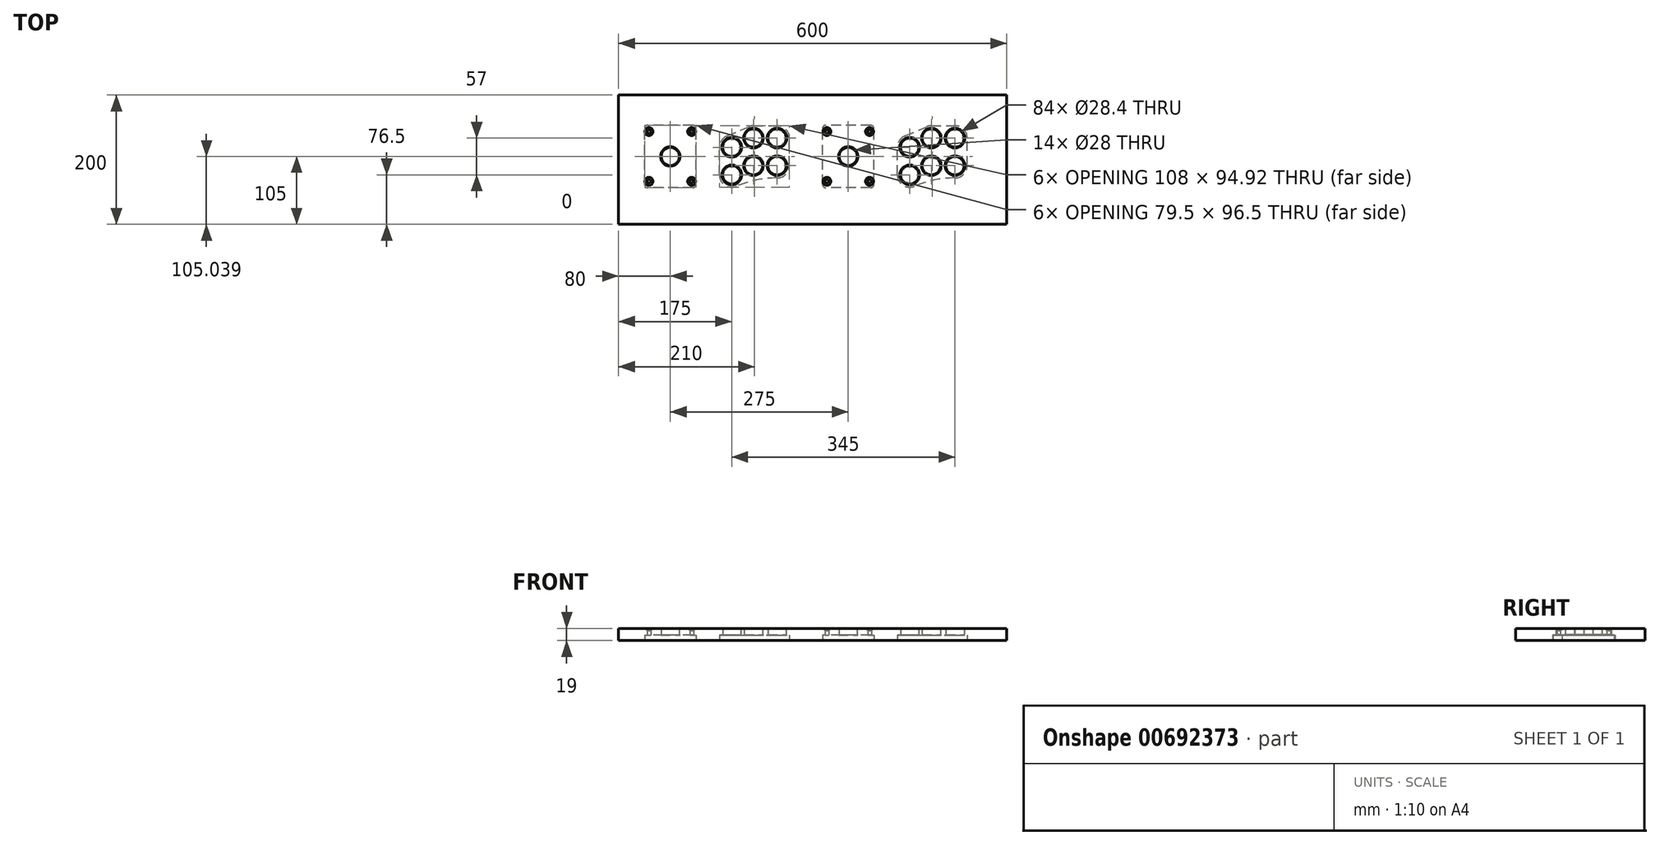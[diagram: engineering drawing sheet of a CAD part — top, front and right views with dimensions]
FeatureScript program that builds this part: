
annotation { "Feature Type Name" : "Feature", "Feature Type Description" : "" }
export const myFeature = defineFeature(function(context is Context, id is Id, definition is map)
    precondition{}
    {
        {
            var Q0;
            Q0=qCreatedBy(makeId("Top.planeOp"),FACE);
            var sketch = newSketch(context, id + "F0", { "sketchPlane" : qUnion([Q0])});
            skLineSegment(sketch, "E0.bottom", {"start": v(-300, 100) * mm, "end": v(300, 100) * mm});
            skLineSegment(sketch, "E0.top", {"start": v(-300, -100) * mm, "end": v(300, -100) * mm});
            skLineSegment(sketch, "E0.left", {"start": v(-300, 100) * mm, "end": v(-300, -100) * mm});
            skLineSegment(sketch, "E0.right", {"start": v(300, 100) * mm, "end": v(300, -100) * mm});
            skPoint(sketch, "E0.middle", {"position": v(0, 0) * mm});
            skLineSegment(sketch, "E1", {"start": v(-300, 19.25) * mm, "end": v(300, 19.25) * mm, "construction": true});
            skLineSegment(sketch, "E2", {"start": v(-300, 33.5) * mm, "end": v(300, 33.5) * mm, "construction": true});
            skLineSegment(sketch, "E3", {"start": v(-300, 5) * mm, "end": v(300, 5) * mm, "construction": true});
            skLineSegment(sketch, "E4", {"start": v(-300, -23.5) * mm, "end": v(300, -23.5) * mm, "construction": true});
            skLineSegment(sketch, "E5", {"start": v(-300, -9.25) * mm, "end": v(300, -9.25) * mm, "construction": true});
            skLineSegment(sketch, "E6", {"start": v(-220, 100) * mm, "end": v(-220, -100) * mm, "construction": true});
            skLineSegment(sketch, "E7", {"start": v(-125, 100) * mm, "end": v(-125, -100) * mm, "construction": true});
            skLineSegment(sketch, "E8", {"start": v(-91.5, 100) * mm, "end": v(-91.5, -100) * mm, "construction": true});
            skLineSegment(sketch, "E9", {"start": v(-55, 100) * mm, "end": v(-55, -100) * mm, "construction": true});
            skCircle(sketch, "E10", {"center": v(-220, 5) * mm, "radius": 14 * mm});
            skCircle(sketch, "E11", {"center": v(-125, 19.25) * mm, "radius": 14.2 * mm});
            skCircle(sketch, "E12", {"center": v(-125, -23.5) * mm, "radius": 14.2 * mm});
            skCircle(sketch, "E13", {"center": v(-91.5, 33.5) * mm, "radius": 14.2 * mm});
            skCircle(sketch, "E14", {"center": v(-91.5, -9.25) * mm, "radius": 14.2 * mm});
            skCircle(sketch, "E15", {"center": v(-55, 33.5) * mm, "radius": 14.2 * mm});
            skCircle(sketch, "E16", {"center": v(-55, -9.25) * mm, "radius": 14.2 * mm});
            skLineSegment(sketch, "E17", {"start": v(55, 100) * mm, "end": v(55, -100) * mm, "construction": true});
            skLineSegment(sketch, "E18", {"start": v(150, 100) * mm, "end": v(150, -100) * mm, "construction": true});
            skLineSegment(sketch, "E19", {"start": v(183.5, 100) * mm, "end": v(183.5, -100) * mm, "construction": true});
            skLineSegment(sketch, "E20", {"start": v(220, 100) * mm, "end": v(220, -100) * mm, "construction": true});
            skLineSegment(sketch, "E21", {"start": v(-220, 90) * mm, "end": v(-300, 90) * mm, "construction": true});
            skLineSegment(sketch, "E22", {"start": v(220, 90) * mm, "end": v(300, 90) * mm, "construction": true});
            skCircle(sketch, "E23", {"center": v(55, 5) * mm, "radius": 14 * mm});
            skCircle(sketch, "E24", {"center": v(150, 19.25) * mm, "radius": 14.2 * mm});
            skCircle(sketch, "E25", {"center": v(150, -23.5) * mm, "radius": 14.2 * mm});
            skCircle(sketch, "E26", {"center": v(183.5, 33.5) * mm, "radius": 14.2 * mm});
            skCircle(sketch, "E27", {"center": v(183.5, -9.25) * mm, "radius": 14.2 * mm});
            skCircle(sketch, "E28", {"center": v(220, -9.25) * mm, "radius": 14.2 * mm});
            skCircle(sketch, "E29", {"center": v(220, 33.5) * mm, "radius": 14.2 * mm});
            skSolve(sketch);
        }
        {
            var Q0;
            Q0=makeQuery(id+"F0.imprint","IMPRINT",FACE,{"disambiguationData":[TD([[makeQuery(id+"F0.imprint","IMPRINT",EDGE,{"derivedFrom":sQuery(id+"F0.wireOp",EDGE,"E0.bottom")}),-1.0]])]});
            extrude(context, id + "F1", {"entities" : qUnion([Q0]), "depth" : 19 * mm, "offsetDistance" : 25 * mm});
        }
        {
            var Q0;
            Q0=makeQuery(id+"F1.opExtrude","CAP_FACE",FACE,{"disambiguationData":[OSD([sQuery(id+"F0.wireOp",EDGE,"E0.bottom"),sQuery(id+"F0.wireOp",EDGE,"E0.top"),sQuery(id+"F0.wireOp",EDGE,"E0.left"),sQuery(id+"F0.wireOp",EDGE,"E0.right"),sQuery(id+"F0.wireOp",EDGE,"E10"),sQuery(id+"F0.wireOp",EDGE,"E11"),sQuery(id+"F0.wireOp",EDGE,"E12"),sQuery(id+"F0.wireOp",EDGE,"E13"),sQuery(id+"F0.wireOp",EDGE,"E14"),sQuery(id+"F0.wireOp",EDGE,"E15"),sQuery(id+"F0.wireOp",EDGE,"E16"),sQuery(id+"F0.wireOp",EDGE,"E23"),sQuery(id+"F0.wireOp",EDGE,"E24"),sQuery(id+"F0.wireOp",EDGE,"E25"),sQuery(id+"F0.wireOp",EDGE,"E26"),sQuery(id+"F0.wireOp",EDGE,"E27"),sQuery(id+"F0.wireOp",EDGE,"E28"),sQuery(id+"F0.wireOp",EDGE,"E29")])],"isStart":true});
            var sketch = newSketch(context, id + "F2", { "sketchPlane" : qUnion([Q0])});
            skLineSegment(sketch, "E30.bottom", {"start": v(-180.25, 43.25) * mm, "end": v(-259.75, 43.25) * mm});
            skLineSegment(sketch, "E30.top", {"start": v(-180.25, -53.25) * mm, "end": v(-259.75, -53.25) * mm});
            skLineSegment(sketch, "E30.left", {"start": v(-180.25, 43.25) * mm, "end": v(-180.25, -53.25) * mm});
            skLineSegment(sketch, "E30.right", {"start": v(-259.75, 43.25) * mm, "end": v(-259.75, -53.25) * mm});
            skPoint(sketch, "E30.middle", {"position": v(-220, -5) * mm});
            skLineSegment(sketch, "E31.bottom", {"start": v(-187, 33.5) * mm, "end": v(-253, 33.5) * mm, "construction": true});
            skLineSegment(sketch, "E31.top", {"start": v(-187, -43.5) * mm, "end": v(-253, -43.5) * mm, "construction": true});
            skLineSegment(sketch, "E31.left", {"start": v(-187, 33.5) * mm, "end": v(-187, -43.5) * mm, "construction": true});
            skLineSegment(sketch, "E31.right", {"start": v(-253, 33.5) * mm, "end": v(-253, -43.5) * mm, "construction": true});
            skCircle(sketch, "E32", {"center": v(-253, 33.5) * mm, "radius": 2.75 * mm});
            skCircle(sketch, "E33", {"center": v(-187, 33.5) * mm, "radius": 2.75 * mm});
            skCircle(sketch, "E34", {"center": v(-187, -43.5) * mm, "radius": 2.75 * mm});
            skCircle(sketch, "E35", {"center": v(-253, -43.5) * mm, "radius": 2.75 * mm});
            skCircle(sketch, "E36", {"center": v(-125, 23.5) * mm, "radius": 19 * mm, "construction": true});
            skCircle(sketch, "E37", {"center": v(-125, -19.25) * mm, "radius": 19 * mm, "construction": true});
            skCircle(sketch, "E38", {"center": v(-91.5, -33.5) * mm, "radius": 19 * mm, "construction": true});
            skCircle(sketch, "E39", {"center": v(-55, -33.5) * mm, "radius": 19 * mm, "construction": true});
            skCircle(sketch, "E40", {"center": v(-55, 9.25) * mm, "radius": 19 * mm, "construction": true});
            skCircle(sketch, "E41", {"center": v(-91.5, 9.25) * mm, "radius": 19 * mm, "construction": true});
            skLineSegment(sketch, "E42", {"start": v(-91.5, -52.5) * mm, "end": v(-55, -52.5) * mm});
            skLineSegment(sketch, "E43", {"start": v(-132.44, -36.73) * mm, "end": v(-98.94, -50.98) * mm});
            skLineSegment(sketch, "E44", {"start": v(-144, 23.5) * mm, "end": v(-144, -19.25) * mm});
            skLineSegment(sketch, "E45", {"start": v(-117.56, 40.98) * mm, "end": v(-84.06, 26.73) * mm, "construction": true});
            skLineSegment(sketch, "E46", {"start": v(-91.5, 28.25) * mm, "end": v(-55, 28.25) * mm, "construction": true});
            skLineSegment(sketch, "E47", {"start": v(-36, 9.25) * mm, "end": v(-36, -33.5) * mm});
            skArc(sketch, "E48", {"start": v(-117.56, 40.98) * mm, "mid": v(-135.48, 39.35) * mm, "end": v(-144, 23.5) * mm});
            skArc(sketch, "E49", {"start": v(-91.5, 28.25) * mm, "mid": v(-95.3, -9.37) * mm, "end": v(-84.06, 26.73) * mm});
            skArc(sketch, "E50", {"start": v(-36, 9.25) * mm, "mid": v(-41.56, 22.69) * mm, "end": v(-55, 28.25) * mm});
            skArc(sketch, "E51", {"start": v(-55, -52.5) * mm, "mid": v(-41.56, -46.94) * mm, "end": v(-36, -33.5) * mm});
            skArc(sketch, "E52", {"start": v(-144, -19.25) * mm, "mid": v(-140.85, -29.73) * mm, "end": v(-132.44, -36.73) * mm});
            skLineSegment(sketch, "E53.bottom", {"start": v(94.75, 43.25) * mm, "end": v(15.25, 43.25) * mm});
            skLineSegment(sketch, "E53.top", {"start": v(94.75, -53.25) * mm, "end": v(15.25, -53.25) * mm});
            skLineSegment(sketch, "E53.left", {"start": v(94.75, 43.25) * mm, "end": v(94.75, -53.25) * mm});
            skLineSegment(sketch, "E53.right", {"start": v(15.25, 43.25) * mm, "end": v(15.25, -53.25) * mm});
            skPoint(sketch, "E53.middle", {"position": v(55, -5) * mm});
            skLineSegment(sketch, "E54.bottom", {"start": v(88, 33.5) * mm, "end": v(22, 33.5) * mm, "construction": true});
            skLineSegment(sketch, "E54.top", {"start": v(88, -43.5) * mm, "end": v(22, -43.5) * mm, "construction": true});
            skLineSegment(sketch, "E54.left", {"start": v(88, 33.5) * mm, "end": v(88, -43.5) * mm, "construction": true});
            skLineSegment(sketch, "E54.right", {"start": v(22, 33.5) * mm, "end": v(22, -43.5) * mm, "construction": true});
            skCircle(sketch, "E55", {"center": v(150, 23.5) * mm, "radius": 19 * mm, "construction": true});
            skCircle(sketch, "E56", {"center": v(183.5, 9.25) * mm, "radius": 19 * mm, "construction": true});
            skCircle(sketch, "E57", {"center": v(220, 9.25) * mm, "radius": 19 * mm, "construction": true});
            skCircle(sketch, "E58", {"center": v(220, -33.5) * mm, "radius": 19 * mm, "construction": true});
            skCircle(sketch, "E59", {"center": v(183.5, -33.5) * mm, "radius": 19 * mm, "construction": true});
            skCircle(sketch, "E60", {"center": v(150, -19.25) * mm, "radius": 19 * mm, "construction": true});
            skCircle(sketch, "E61", {"center": v(22, 33.5) * mm, "radius": 2.75 * mm});
            skCircle(sketch, "E62", {"center": v(88, 33.5) * mm, "radius": 2.75 * mm});
            skCircle(sketch, "E63", {"center": v(88, -43.5) * mm, "radius": 2.75 * mm});
            skCircle(sketch, "E64", {"center": v(22, -43.5) * mm, "radius": 2.75 * mm});
            skLineSegment(sketch, "E65", {"start": v(142.56, -36.73) * mm, "end": v(176.06, -50.98) * mm});
            skLineSegment(sketch, "E66", {"start": v(183.5, -52.5) * mm, "end": v(220, -52.5) * mm});
            skLineSegment(sketch, "E67", {"start": v(131, 23.5) * mm, "end": v(131, -19.25) * mm});
            skLineSegment(sketch, "E68", {"start": v(157.44, 40.98) * mm, "end": v(190.94, 26.73) * mm, "construction": true});
            skLineSegment(sketch, "E69", {"start": v(183.5, 28.25) * mm, "end": v(220, 28.25) * mm, "construction": true});
            skLineSegment(sketch, "E70", {"start": v(239, 9.25) * mm, "end": v(239, -33.5) * mm});
            skArc(sketch, "E71", {"start": v(220, -52.5) * mm, "mid": v(233.44, -46.94) * mm, "end": v(239, -33.5) * mm});
            skArc(sketch, "E72", {"start": v(239, 9.25) * mm, "mid": v(233.44, 22.69) * mm, "end": v(220, 28.25) * mm});
            skArc(sketch, "E73", {"start": v(183.5, 28.25) * mm, "mid": v(179.7, -9.37) * mm, "end": v(190.94, 26.73) * mm});
            skArc(sketch, "E74", {"start": v(157.44, 40.98) * mm, "mid": v(139.52, 39.35) * mm, "end": v(131, 23.5) * mm});
            skArc(sketch, "E75", {"start": v(131, -19.25) * mm, "mid": v(134.15, -29.73) * mm, "end": v(142.56, -36.73) * mm});
            skArc(sketch, "E76", {"start": v(-117.56, 40.98) * mm, "mid": v(-86.92, 31.47) * mm, "end": v(-55, 28.25) * mm});
            skArc(sketch, "E77", {"start": v(-98.94, -50.98) * mm, "mid": v(-95.3, -52.12) * mm, "end": v(-91.5, -52.5) * mm});
            skArc(sketch, "E78", {"start": v(157.44, 40.98) * mm, "mid": v(188.08, 31.47) * mm, "end": v(220, 28.25) * mm});
            skArc(sketch, "E79", {"start": v(176.06, -50.98) * mm, "mid": v(179.7, -52.12) * mm, "end": v(183.5, -52.5) * mm});
            skSolve(sketch);
        }
        {
            var Q0;
            Q0=makeQuery(id+"F2.imprint","IMPRINT",FACE,{"disambiguationData":[TD([[makeQuery(id+"F2.imprint","IMPRINT",EDGE,{"derivedFrom":sQuery(id+"F2.wireOp",EDGE,"E44")}),1.0]])]});
            var Q1;
            Q1=makeQuery(id+"F2.imprint","IMPRINT",FACE,{"disambiguationData":[TD([[makeQuery(id+"F2.imprint","IMPRINT",EDGE,{"derivedFrom":sQuery(id+"F2.wireOp",EDGE,"E32")}),1.0]])]});
            var Q2;
            Q2=makeQuery(id+"F2.imprint","IMPRINT",FACE,{"disambiguationData":[TD([[makeQuery(id+"F2.imprint","IMPRINT",EDGE,{"derivedFrom":sQuery(id+"F2.wireOp",EDGE,"E33")}),1.0]])]});
            var Q3;
            Q3=makeQuery(id+"F2.imprint","IMPRINT",FACE,{"disambiguationData":[TD([[makeQuery(id+"F2.imprint","IMPRINT",EDGE,{"derivedFrom":sQuery(id+"F2.wireOp",EDGE,"E34")}),1.0]])]});
            var Q4;
            Q4=makeQuery(id+"F2.imprint","IMPRINT",FACE,{"disambiguationData":[TD([[makeQuery(id+"F2.imprint","IMPRINT",EDGE,{"derivedFrom":sQuery(id+"F2.wireOp",EDGE,"E35")}),1.0]])]});
            var Q5;
            Q5=makeQuery(id+"F2.imprint","IMPRINT",FACE,{"disambiguationData":[TD([[makeQuery(id+"F2.imprint","IMPRINT",EDGE,{"derivedFrom":sQuery(id+"F2.wireOp",EDGE,"E30.bottom")}),1.0]])]});
            var Q6;
            Q6=makeQuery(id+"F2.imprint","IMPRINT",FACE,{"disambiguationData":[TD([[makeQuery(id+"F2.imprint","IMPRINT",EDGE,{"derivedFrom":sQuery(id+"F2.wireOp",EDGE,"E61")}),1.0]])]});
            var Q7;
            Q7=makeQuery(id+"F2.imprint","IMPRINT",FACE,{"disambiguationData":[TD([[makeQuery(id+"F2.imprint","IMPRINT",EDGE,{"derivedFrom":sQuery(id+"F2.wireOp",EDGE,"E62")}),1.0]])]});
            var Q8;
            Q8=makeQuery(id+"F2.imprint","IMPRINT",FACE,{"disambiguationData":[TD([[makeQuery(id+"F2.imprint","IMPRINT",EDGE,{"derivedFrom":sQuery(id+"F2.wireOp",EDGE,"E63")}),1.0]])]});
            var Q9;
            Q9=makeQuery(id+"F2.imprint","IMPRINT",FACE,{"disambiguationData":[TD([[makeQuery(id+"F2.imprint","IMPRINT",EDGE,{"derivedFrom":sQuery(id+"F2.wireOp",EDGE,"E64")}),1.0]])]});
            var Q10;
            Q10=makeQuery(id+"F2.imprint","IMPRINT",FACE,{"disambiguationData":[TD([[makeQuery(id+"F2.imprint","IMPRINT",EDGE,{"derivedFrom":sQuery(id+"F2.wireOp",EDGE,"E53.bottom")}),1.0]])]});
            var Q11;
            Q11=makeQuery(id+"F2.imprint","IMPRINT",FACE,{"disambiguationData":[TD([[makeQuery(id+"F2.imprint","IMPRINT",EDGE,{"derivedFrom":sQuery(id+"F2.wireOp",EDGE,"E67")}),1.0]])]});
            extrude(context, id + "F3", {"entities" : qUnion([Q0, Q1, Q2, Q3, Q4, Q5, Q6, Q7, Q8, Q9, Q10, Q11]), "operationType" : NewBodyOperationType.REMOVE, "oppositeDirection" : true, "depth" : 8.5 * mm, "offsetDistance" : 25 * mm});
        }
        {
            var Q0;
            Q0=makeQuery(id+"F2.imprint","IMPRINT",FACE,{"disambiguationData":[TD([[makeQuery(id+"F2.imprint","IMPRINT",EDGE,{"derivedFrom":sQuery(id+"F2.wireOp",EDGE,"E32")}),1.0]])]});
            var Q1;
            Q1=makeQuery(id+"F2.imprint","IMPRINT",FACE,{"disambiguationData":[TD([[makeQuery(id+"F2.imprint","IMPRINT",EDGE,{"derivedFrom":sQuery(id+"F2.wireOp",EDGE,"E33")}),1.0]])]});
            var Q2;
            Q2=makeQuery(id+"F2.imprint","IMPRINT",FACE,{"disambiguationData":[TD([[makeQuery(id+"F2.imprint","IMPRINT",EDGE,{"derivedFrom":sQuery(id+"F2.wireOp",EDGE,"E34")}),1.0]])]});
            var Q3;
            Q3=makeQuery(id+"F2.imprint","IMPRINT",FACE,{"disambiguationData":[TD([[makeQuery(id+"F2.imprint","IMPRINT",EDGE,{"derivedFrom":sQuery(id+"F2.wireOp",EDGE,"E35")}),1.0]])]});
            var Q4;
            Q4=makeQuery(id+"F2.imprint","IMPRINT",FACE,{"disambiguationData":[TD([[makeQuery(id+"F2.imprint","IMPRINT",EDGE,{"derivedFrom":sQuery(id+"F2.wireOp",EDGE,"E61")}),1.0]])]});
            var Q5;
            Q5=makeQuery(id+"F2.imprint","IMPRINT",FACE,{"disambiguationData":[TD([[makeQuery(id+"F2.imprint","IMPRINT",EDGE,{"derivedFrom":sQuery(id+"F2.wireOp",EDGE,"E62")}),1.0]])]});
            var Q6;
            Q6=makeQuery(id+"F2.imprint","IMPRINT",FACE,{"disambiguationData":[TD([[makeQuery(id+"F2.imprint","IMPRINT",EDGE,{"derivedFrom":sQuery(id+"F2.wireOp",EDGE,"E63")}),1.0]])]});
            var Q7;
            Q7=makeQuery(id+"F2.imprint","IMPRINT",FACE,{"disambiguationData":[TD([[makeQuery(id+"F2.imprint","IMPRINT",EDGE,{"derivedFrom":sQuery(id+"F2.wireOp",EDGE,"E64")}),1.0]])]});
            extrude(context, id + "F4", {"entities" : qUnion([Q0, Q1, Q2, Q3, Q4, Q5, Q6, Q7]), "operationType" : NewBodyOperationType.REMOVE, "endBound" : BoundingType.THROUGH_ALL, "oppositeDirection" : true, "depth" : 25 * mm, "offsetDistance" : 25 * mm});
        }
        {
            var Q0;
            Q0=makeQuery(id+"F3.boolean.opBoolean","COPY",EDGE,{"derivedFrom":makeQuery(id+"F3.opExtrude","SWEPT_EDGE",EDGE,{"disambiguationData":[OSD([sQuery(id+"F2.wireOp",EDGE,"E30.bottom"),sQuery(id+"F2.wireOp",EDGE,"E30.right")])]})});
            var Q1;
            Q1=makeQuery(id+"F3.boolean.opBoolean","COPY",EDGE,{"derivedFrom":makeQuery(id+"F3.opExtrude","SWEPT_EDGE",EDGE,{"disambiguationData":[OSD([sQuery(id+"F2.wireOp",EDGE,"E30.bottom"),sQuery(id+"F2.wireOp",EDGE,"E30.left")])]})});
            var Q2;
            Q2=makeQuery(id+"F3.boolean.opBoolean","COPY",EDGE,{"derivedFrom":makeQuery(id+"F3.opExtrude","SWEPT_EDGE",EDGE,{"disambiguationData":[OSD([sQuery(id+"F2.wireOp",EDGE,"E30.top"),sQuery(id+"F2.wireOp",EDGE,"E30.left")])]})});
            var Q3;
            Q3=makeQuery(id+"F3.boolean.opBoolean","COPY",EDGE,{"derivedFrom":makeQuery(id+"F3.opExtrude","SWEPT_EDGE",EDGE,{"disambiguationData":[OSD([sQuery(id+"F2.wireOp",EDGE,"E30.top"),sQuery(id+"F2.wireOp",EDGE,"E30.right")])]})});
            var Q4;
            Q4=makeQuery(id+"F3.boolean.opBoolean","COPY",EDGE,{"derivedFrom":makeQuery(id+"F3.opExtrude","SWEPT_EDGE",EDGE,{"disambiguationData":[OSD([sQuery(id+"F2.wireOp",EDGE,"E53.top"),sQuery(id+"F2.wireOp",EDGE,"E53.right")])]})});
            var Q5;
            Q5=makeQuery(id+"F3.boolean.opBoolean","COPY",EDGE,{"derivedFrom":makeQuery(id+"F3.opExtrude","SWEPT_EDGE",EDGE,{"disambiguationData":[OSD([sQuery(id+"F2.wireOp",EDGE,"E53.bottom"),sQuery(id+"F2.wireOp",EDGE,"E53.right")])]})});
            var Q6;
            Q6=makeQuery(id+"F3.boolean.opBoolean","COPY",EDGE,{"derivedFrom":makeQuery(id+"F3.opExtrude","SWEPT_EDGE",EDGE,{"disambiguationData":[OSD([sQuery(id+"F2.wireOp",EDGE,"E53.bottom"),sQuery(id+"F2.wireOp",EDGE,"E53.left")])]})});
            var Q7;
            Q7=makeQuery(id+"F3.boolean.opBoolean","COPY",EDGE,{"derivedFrom":makeQuery(id+"F3.opExtrude","SWEPT_EDGE",EDGE,{"disambiguationData":[OSD([sQuery(id+"F2.wireOp",EDGE,"E53.top"),sQuery(id+"F2.wireOp",EDGE,"E53.left")])]})});
            fillet(context, id + "F5", {"entities" : qUnion([Q0, Q1, Q2, Q3, Q4, Q5, Q6, Q7]), "radius" : 5 * mm, "tangentPropagation" : true, "allowEdgeOverflow" : false});
        }
        {
            var Q0;
            Q0=makeQuery(id+"F4.boolean.opBoolean","INTERSECT",EDGE,{"derivedFrom":[makeQuery(id+"F1.opExtrude","CAP_FACE",FACE,{"disambiguationData":[OSD([sQuery(id+"F0.wireOp",EDGE,"E0.bottom"),sQuery(id+"F0.wireOp",EDGE,"E0.top"),sQuery(id+"F0.wireOp",EDGE,"E0.left"),sQuery(id+"F0.wireOp",EDGE,"E0.right"),sQuery(id+"F0.wireOp",EDGE,"E10"),sQuery(id+"F0.wireOp",EDGE,"E11"),sQuery(id+"F0.wireOp",EDGE,"E12"),sQuery(id+"F0.wireOp",EDGE,"E13"),sQuery(id+"F0.wireOp",EDGE,"E14"),sQuery(id+"F0.wireOp",EDGE,"E15"),sQuery(id+"F0.wireOp",EDGE,"E16"),sQuery(id+"F0.wireOp",EDGE,"E23"),sQuery(id+"F0.wireOp",EDGE,"E24"),sQuery(id+"F0.wireOp",EDGE,"E25"),sQuery(id+"F0.wireOp",EDGE,"E26"),sQuery(id+"F0.wireOp",EDGE,"E27"),sQuery(id+"F0.wireOp",EDGE,"E28"),sQuery(id+"F0.wireOp",EDGE,"E29")])],"isStart":false}),makeQuery(id+"F4.opExtrude","SWEPT_FACE",FACE,{"disambiguationData":[OSD([sQuery(id+"F2.wireOp",EDGE,"E62")])]})]});
            var Q1;
            Q1=makeQuery(id+"F4.boolean.opBoolean","INTERSECT",EDGE,{"derivedFrom":[makeQuery(id+"F1.opExtrude","CAP_FACE",FACE,{"disambiguationData":[OSD([sQuery(id+"F0.wireOp",EDGE,"E0.bottom"),sQuery(id+"F0.wireOp",EDGE,"E0.top"),sQuery(id+"F0.wireOp",EDGE,"E0.left"),sQuery(id+"F0.wireOp",EDGE,"E0.right"),sQuery(id+"F0.wireOp",EDGE,"E10"),sQuery(id+"F0.wireOp",EDGE,"E11"),sQuery(id+"F0.wireOp",EDGE,"E12"),sQuery(id+"F0.wireOp",EDGE,"E13"),sQuery(id+"F0.wireOp",EDGE,"E14"),sQuery(id+"F0.wireOp",EDGE,"E15"),sQuery(id+"F0.wireOp",EDGE,"E16"),sQuery(id+"F0.wireOp",EDGE,"E23"),sQuery(id+"F0.wireOp",EDGE,"E24"),sQuery(id+"F0.wireOp",EDGE,"E25"),sQuery(id+"F0.wireOp",EDGE,"E26"),sQuery(id+"F0.wireOp",EDGE,"E27"),sQuery(id+"F0.wireOp",EDGE,"E28"),sQuery(id+"F0.wireOp",EDGE,"E29")])],"isStart":false}),makeQuery(id+"F4.opExtrude","SWEPT_FACE",FACE,{"disambiguationData":[OSD([sQuery(id+"F2.wireOp",EDGE,"E63")])]})]});
            var Q2;
            Q2=makeQuery(id+"F4.boolean.opBoolean","INTERSECT",EDGE,{"derivedFrom":[makeQuery(id+"F1.opExtrude","CAP_FACE",FACE,{"disambiguationData":[OSD([sQuery(id+"F0.wireOp",EDGE,"E0.bottom"),sQuery(id+"F0.wireOp",EDGE,"E0.top"),sQuery(id+"F0.wireOp",EDGE,"E0.left"),sQuery(id+"F0.wireOp",EDGE,"E0.right"),sQuery(id+"F0.wireOp",EDGE,"E10"),sQuery(id+"F0.wireOp",EDGE,"E11"),sQuery(id+"F0.wireOp",EDGE,"E12"),sQuery(id+"F0.wireOp",EDGE,"E13"),sQuery(id+"F0.wireOp",EDGE,"E14"),sQuery(id+"F0.wireOp",EDGE,"E15"),sQuery(id+"F0.wireOp",EDGE,"E16"),sQuery(id+"F0.wireOp",EDGE,"E23"),sQuery(id+"F0.wireOp",EDGE,"E24"),sQuery(id+"F0.wireOp",EDGE,"E25"),sQuery(id+"F0.wireOp",EDGE,"E26"),sQuery(id+"F0.wireOp",EDGE,"E27"),sQuery(id+"F0.wireOp",EDGE,"E28"),sQuery(id+"F0.wireOp",EDGE,"E29")])],"isStart":false}),makeQuery(id+"F4.opExtrude","SWEPT_FACE",FACE,{"disambiguationData":[OSD([sQuery(id+"F2.wireOp",EDGE,"E64")])]})]});
            var Q3;
            Q3=makeQuery(id+"F4.boolean.opBoolean","INTERSECT",EDGE,{"derivedFrom":[makeQuery(id+"F1.opExtrude","CAP_FACE",FACE,{"disambiguationData":[OSD([sQuery(id+"F0.wireOp",EDGE,"E0.bottom"),sQuery(id+"F0.wireOp",EDGE,"E0.top"),sQuery(id+"F0.wireOp",EDGE,"E0.left"),sQuery(id+"F0.wireOp",EDGE,"E0.right"),sQuery(id+"F0.wireOp",EDGE,"E10"),sQuery(id+"F0.wireOp",EDGE,"E11"),sQuery(id+"F0.wireOp",EDGE,"E12"),sQuery(id+"F0.wireOp",EDGE,"E13"),sQuery(id+"F0.wireOp",EDGE,"E14"),sQuery(id+"F0.wireOp",EDGE,"E15"),sQuery(id+"F0.wireOp",EDGE,"E16"),sQuery(id+"F0.wireOp",EDGE,"E23"),sQuery(id+"F0.wireOp",EDGE,"E24"),sQuery(id+"F0.wireOp",EDGE,"E25"),sQuery(id+"F0.wireOp",EDGE,"E26"),sQuery(id+"F0.wireOp",EDGE,"E27"),sQuery(id+"F0.wireOp",EDGE,"E28"),sQuery(id+"F0.wireOp",EDGE,"E29")])],"isStart":false}),makeQuery(id+"F4.opExtrude","SWEPT_FACE",FACE,{"disambiguationData":[OSD([sQuery(id+"F2.wireOp",EDGE,"E61")])]})]});
            var Q4;
            Q4=makeQuery(id+"F4.boolean.opBoolean","INTERSECT",EDGE,{"derivedFrom":[makeQuery(id+"F1.opExtrude","CAP_FACE",FACE,{"disambiguationData":[OSD([sQuery(id+"F0.wireOp",EDGE,"E0.bottom"),sQuery(id+"F0.wireOp",EDGE,"E0.top"),sQuery(id+"F0.wireOp",EDGE,"E0.left"),sQuery(id+"F0.wireOp",EDGE,"E0.right"),sQuery(id+"F0.wireOp",EDGE,"E10"),sQuery(id+"F0.wireOp",EDGE,"E11"),sQuery(id+"F0.wireOp",EDGE,"E12"),sQuery(id+"F0.wireOp",EDGE,"E13"),sQuery(id+"F0.wireOp",EDGE,"E14"),sQuery(id+"F0.wireOp",EDGE,"E15"),sQuery(id+"F0.wireOp",EDGE,"E16"),sQuery(id+"F0.wireOp",EDGE,"E23"),sQuery(id+"F0.wireOp",EDGE,"E24"),sQuery(id+"F0.wireOp",EDGE,"E25"),sQuery(id+"F0.wireOp",EDGE,"E26"),sQuery(id+"F0.wireOp",EDGE,"E27"),sQuery(id+"F0.wireOp",EDGE,"E28"),sQuery(id+"F0.wireOp",EDGE,"E29")])],"isStart":false}),makeQuery(id+"F4.opExtrude","SWEPT_FACE",FACE,{"disambiguationData":[OSD([sQuery(id+"F2.wireOp",EDGE,"E34")])]})]});
            var Q5;
            Q5=makeQuery(id+"F4.boolean.opBoolean","INTERSECT",EDGE,{"derivedFrom":[makeQuery(id+"F1.opExtrude","CAP_FACE",FACE,{"disambiguationData":[OSD([sQuery(id+"F0.wireOp",EDGE,"E0.bottom"),sQuery(id+"F0.wireOp",EDGE,"E0.top"),sQuery(id+"F0.wireOp",EDGE,"E0.left"),sQuery(id+"F0.wireOp",EDGE,"E0.right"),sQuery(id+"F0.wireOp",EDGE,"E10"),sQuery(id+"F0.wireOp",EDGE,"E11"),sQuery(id+"F0.wireOp",EDGE,"E12"),sQuery(id+"F0.wireOp",EDGE,"E13"),sQuery(id+"F0.wireOp",EDGE,"E14"),sQuery(id+"F0.wireOp",EDGE,"E15"),sQuery(id+"F0.wireOp",EDGE,"E16"),sQuery(id+"F0.wireOp",EDGE,"E23"),sQuery(id+"F0.wireOp",EDGE,"E24"),sQuery(id+"F0.wireOp",EDGE,"E25"),sQuery(id+"F0.wireOp",EDGE,"E26"),sQuery(id+"F0.wireOp",EDGE,"E27"),sQuery(id+"F0.wireOp",EDGE,"E28"),sQuery(id+"F0.wireOp",EDGE,"E29")])],"isStart":false}),makeQuery(id+"F4.opExtrude","SWEPT_FACE",FACE,{"disambiguationData":[OSD([sQuery(id+"F2.wireOp",EDGE,"E33")])]})]});
            var Q6;
            Q6=makeQuery(id+"F4.boolean.opBoolean","INTERSECT",EDGE,{"derivedFrom":[makeQuery(id+"F1.opExtrude","CAP_FACE",FACE,{"disambiguationData":[OSD([sQuery(id+"F0.wireOp",EDGE,"E0.bottom"),sQuery(id+"F0.wireOp",EDGE,"E0.top"),sQuery(id+"F0.wireOp",EDGE,"E0.left"),sQuery(id+"F0.wireOp",EDGE,"E0.right"),sQuery(id+"F0.wireOp",EDGE,"E10"),sQuery(id+"F0.wireOp",EDGE,"E11"),sQuery(id+"F0.wireOp",EDGE,"E12"),sQuery(id+"F0.wireOp",EDGE,"E13"),sQuery(id+"F0.wireOp",EDGE,"E14"),sQuery(id+"F0.wireOp",EDGE,"E15"),sQuery(id+"F0.wireOp",EDGE,"E16"),sQuery(id+"F0.wireOp",EDGE,"E23"),sQuery(id+"F0.wireOp",EDGE,"E24"),sQuery(id+"F0.wireOp",EDGE,"E25"),sQuery(id+"F0.wireOp",EDGE,"E26"),sQuery(id+"F0.wireOp",EDGE,"E27"),sQuery(id+"F0.wireOp",EDGE,"E28"),sQuery(id+"F0.wireOp",EDGE,"E29")])],"isStart":false}),makeQuery(id+"F4.opExtrude","SWEPT_FACE",FACE,{"disambiguationData":[OSD([sQuery(id+"F2.wireOp",EDGE,"E32")])]})]});
            var Q7;
            Q7=makeQuery(id+"F4.boolean.opBoolean","INTERSECT",EDGE,{"derivedFrom":[makeQuery(id+"F1.opExtrude","CAP_FACE",FACE,{"disambiguationData":[OSD([sQuery(id+"F0.wireOp",EDGE,"E0.bottom"),sQuery(id+"F0.wireOp",EDGE,"E0.top"),sQuery(id+"F0.wireOp",EDGE,"E0.left"),sQuery(id+"F0.wireOp",EDGE,"E0.right"),sQuery(id+"F0.wireOp",EDGE,"E10"),sQuery(id+"F0.wireOp",EDGE,"E11"),sQuery(id+"F0.wireOp",EDGE,"E12"),sQuery(id+"F0.wireOp",EDGE,"E13"),sQuery(id+"F0.wireOp",EDGE,"E14"),sQuery(id+"F0.wireOp",EDGE,"E15"),sQuery(id+"F0.wireOp",EDGE,"E16"),sQuery(id+"F0.wireOp",EDGE,"E23"),sQuery(id+"F0.wireOp",EDGE,"E24"),sQuery(id+"F0.wireOp",EDGE,"E25"),sQuery(id+"F0.wireOp",EDGE,"E26"),sQuery(id+"F0.wireOp",EDGE,"E27"),sQuery(id+"F0.wireOp",EDGE,"E28"),sQuery(id+"F0.wireOp",EDGE,"E29")])],"isStart":false}),makeQuery(id+"F4.opExtrude","SWEPT_FACE",FACE,{"disambiguationData":[OSD([sQuery(id+"F2.wireOp",EDGE,"E35")])]})]});
            chamfer(context, id + "F6", {"entities" : qUnion([Q0, Q1, Q2, Q3, Q4, Q5, Q6, Q7]), "width" : 3.5 * mm, "tangentPropagation" : true});
        }
        {
            var Q0;
            Q0=makeQuery(id+"F1.opExtrude","SWEPT_FACE",FACE,{"disambiguationData":[OSD([sQuery(id+"F0.wireOp",EDGE,"E10")])]});
            var Q1;
            Q1=makeQuery(id+"F1.opExtrude","SWEPT_FACE",FACE,{"disambiguationData":[OSD([sQuery(id+"F0.wireOp",EDGE,"E11")])]});
            var Q2;
            Q2=makeQuery(id+"F1.opExtrude","SWEPT_FACE",FACE,{"disambiguationData":[OSD([sQuery(id+"F0.wireOp",EDGE,"E13")])]});
            var Q3;
            Q3=makeQuery(id+"F1.opExtrude","SWEPT_FACE",FACE,{"disambiguationData":[OSD([sQuery(id+"F0.wireOp",EDGE,"E12")])]});
            var Q4;
            Q4=makeQuery(id+"F1.opExtrude","SWEPT_FACE",FACE,{"disambiguationData":[OSD([sQuery(id+"F0.wireOp",EDGE,"E14")])]});
            var Q5;
            Q5=makeQuery(id+"F1.opExtrude","SWEPT_FACE",FACE,{"disambiguationData":[OSD([sQuery(id+"F0.wireOp",EDGE,"E16")])]});
            var Q6;
            Q6=makeQuery(id+"F1.opExtrude","SWEPT_FACE",FACE,{"disambiguationData":[OSD([sQuery(id+"F0.wireOp",EDGE,"E15")])]});
            var Q7;
            Q7=makeQuery(id+"F1.opExtrude","SWEPT_FACE",FACE,{"disambiguationData":[OSD([sQuery(id+"F0.wireOp",EDGE,"E23")])]});
            var Q8;
            Q8=makeQuery(id+"F1.opExtrude","SWEPT_FACE",FACE,{"disambiguationData":[OSD([sQuery(id+"F0.wireOp",EDGE,"E24")])]});
            var Q9;
            Q9=makeQuery(id+"F1.opExtrude","SWEPT_FACE",FACE,{"disambiguationData":[OSD([sQuery(id+"F0.wireOp",EDGE,"E25")])]});
            var Q10;
            Q10=makeQuery(id+"F1.opExtrude","SWEPT_FACE",FACE,{"disambiguationData":[OSD([sQuery(id+"F0.wireOp",EDGE,"E27")])]});
            var Q11;
            Q11=makeQuery(id+"F1.opExtrude","SWEPT_FACE",FACE,{"disambiguationData":[OSD([sQuery(id+"F0.wireOp",EDGE,"E26")])]});
            var Q12;
            Q12=makeQuery(id+"F1.opExtrude","SWEPT_FACE",FACE,{"disambiguationData":[OSD([sQuery(id+"F0.wireOp",EDGE,"E29")])]});
            var Q13;
            Q13=makeQuery(id+"F1.opExtrude","SWEPT_FACE",FACE,{"disambiguationData":[OSD([sQuery(id+"F0.wireOp",EDGE,"E28")])]});
            var Q14;
            Q14=makeQuery(id+"F3.boolean.opBoolean","COPY",EDGE,{"derivedFrom":makeQuery(id+"F3.opExtrude","CAP_EDGE",EDGE,{"disambiguationData":[OSD([sQuery(id+"F2.wireOp",EDGE,"RX0PKqlT-ShXH-tcj8-fC1a-jLyNVPEMgFMR")])],"isStart":true})});
            var Q15;
            Q15=makeQuery(id+"F3.boolean.opBoolean","COPY",EDGE,{"derivedFrom":makeQuery(id+"F3.opExtrude","CAP_EDGE",EDGE,{"disambiguationData":[OSD([sQuery(id+"F2.wireOp",EDGE,"E53.top")])],"isStart":true})});
            var Q16;
            Q16=makeQuery(id+"F3.boolean.opBoolean","COPY",EDGE,{"derivedFrom":makeQuery(id+"F3.opExtrude","CAP_EDGE",EDGE,{"disambiguationData":[OSD([sQuery(id+"F2.wireOp",EDGE,"N9enReF0-IvZI-JQNr-NccO-0kK5CmvpcBLG")])],"isStart":true})});
            var Q17;
            Q17=makeQuery(id+"F3.boolean.opBoolean","COPY",EDGE,{"derivedFrom":makeQuery(id+"F3.opExtrude","CAP_EDGE",EDGE,{"disambiguationData":[OSD([sQuery(id+"F2.wireOp",EDGE,"E30.top")])],"isStart":true})});
            var Q18;
            Q18=makeQuery(id+"F3.boolean.opBoolean","COPY",EDGE,{"derivedFrom":makeQuery(id+"F3.opExtrude","CAP_EDGE",EDGE,{"disambiguationData":[OSD([sQuery(id+"F2.wireOp",EDGE,"E76")])],"isStart":true})});
            var Q19;
            Q19=makeQuery(id+"F3.boolean.opBoolean","COPY",EDGE,{"derivedFrom":makeQuery(id+"F3.opExtrude","CAP_EDGE",EDGE,{"disambiguationData":[OSD([sQuery(id+"F2.wireOp",EDGE,"E78")])],"isStart":true})});
            chamfer(context, id + "F7", {"entities" : qUnion([Q0, Q1, Q2, Q3, Q4, Q5, Q6, Q7, Q8, Q9, Q10, Q11, Q12, Q13, Q14, Q15, Q16, Q17, Q18, Q19]), "width" : 1 * mm, "tangentPropagation" : true});
        }
    });
